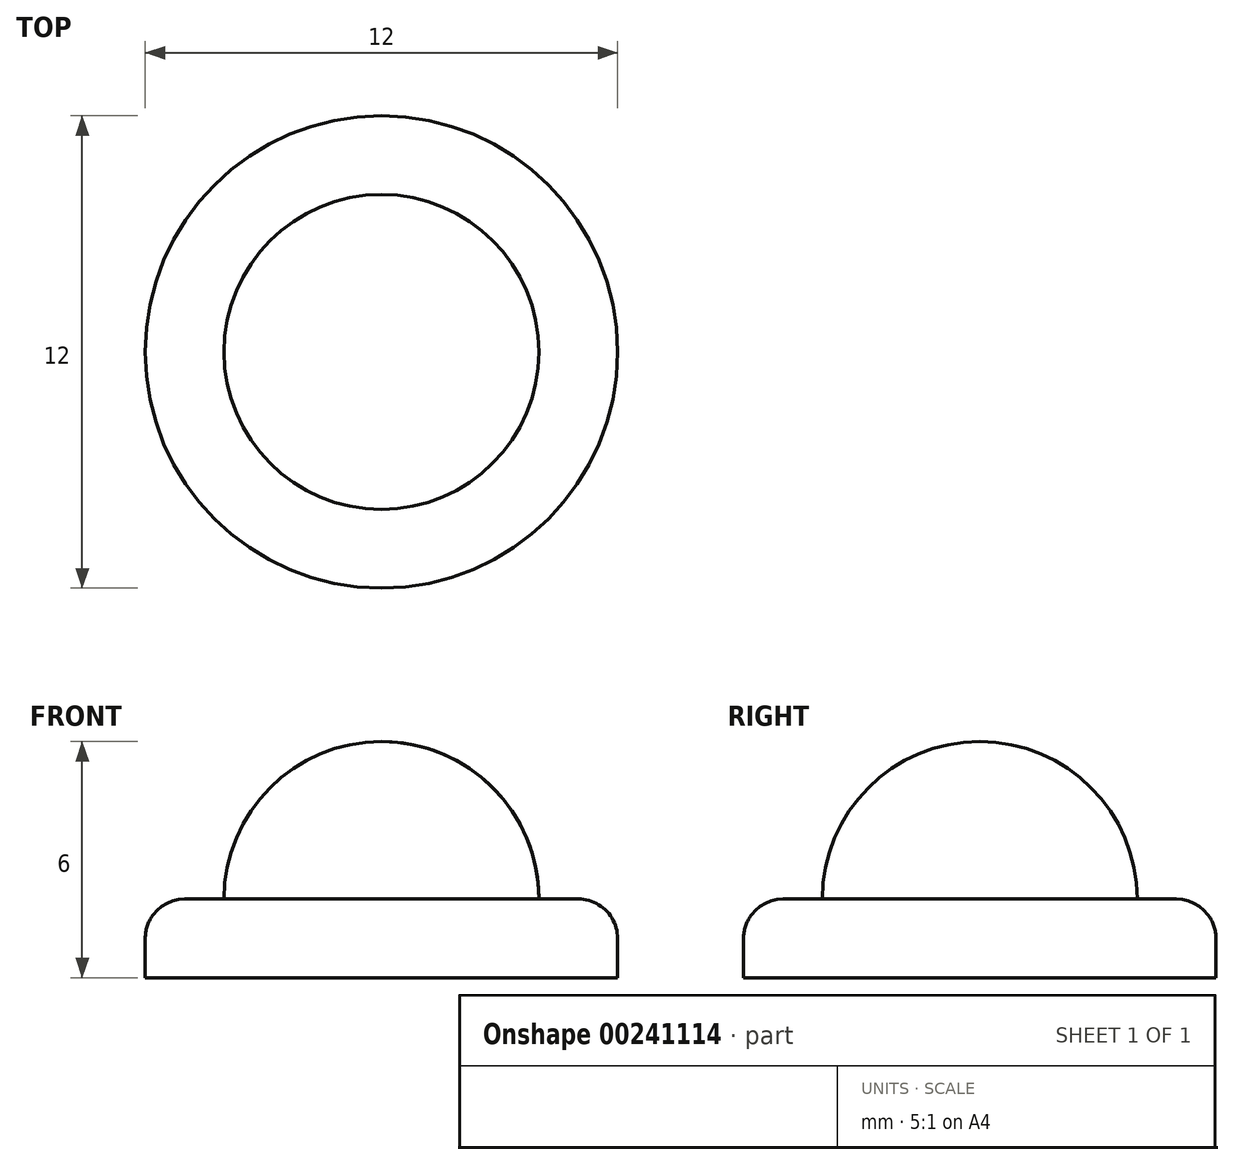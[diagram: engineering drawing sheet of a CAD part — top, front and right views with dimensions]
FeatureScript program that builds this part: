
annotation { "Feature Type Name" : "Feature", "Feature Type Description" : "" }
export const myFeature = defineFeature(function(context is Context, id is Id, definition is map)
    precondition{}
    {
        {
            var Q0;
            Q0=qCreatedBy(makeId("Top.planeOp"),FACE);
            var sketch = newSketch(context, id + "F0", { "sketchPlane" : qUnion([Q0])});
            skCircle(sketch, "E0", {"center": v(0, 0) * mm, "radius": 4 * mm});
            skSolve(sketch);
        }
        {
            var Q0;
            Q0 = qSketchRegion(id + "F0", true);
            extrude(context, id + "F1", {"entities" : qUnion([Q0]), "depth" : 4 * mm});
        }
        {
            var Q0;
            Q0=makeQuery(id+"F1.opExtrude","CAP_EDGE",EDGE,{"disambiguationData":[OSD([sQuery(id+"F0.wireOp",EDGE,"E0")])],"isStart":false});
            fillet(context, id + "F2", {"entities" : qUnion([Q0]), "radius" : 4 * mm, "tangentPropagation" : true, "allowEdgeOverflow" : false});
        }
        {
            var Q0;
            Q0=qCreatedBy(makeId("Top.planeOp"),FACE);
            var sketch = newSketch(context, id + "F3", { "sketchPlane" : qUnion([Q0])});
            skCircle(sketch, "E1", {"center": v(0, 0) * mm, "radius": 6 * mm});
            skSolve(sketch);
        }
        {
            var Q0;
            Q0 = qSketchRegion(id + "F3", true);
            extrude(context, id + "F4", {"entities" : qUnion([Q0]), "oppositeDirection" : true, "depth" : 2 * mm});
        }
        {
            var Q0;
            Q0=makeQuery(id+"F4.opExtrude","CAP_EDGE",EDGE,{"disambiguationData":[OSD([sQuery(id+"F3.wireOp",EDGE,"E1")])],"isStart":true});
            fillet(context, id + "F5", {"entities" : qUnion([Q0]), "radius" : 1 * mm, "tangentPropagation" : true, "allowEdgeOverflow" : false});
        }
    });
